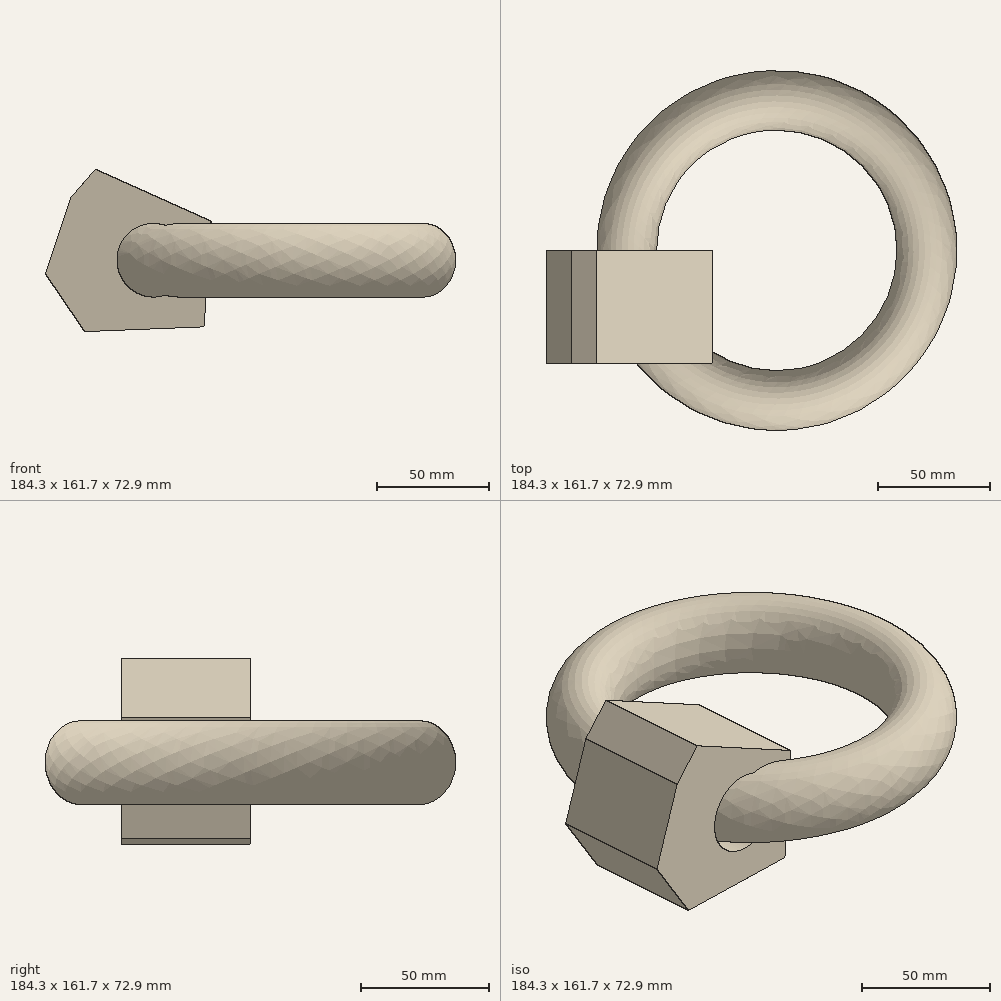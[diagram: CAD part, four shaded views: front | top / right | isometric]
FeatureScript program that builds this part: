
annotation { "Feature Type Name" : "Feature", "Feature Type Description" : "" }
export const myFeature = defineFeature(function(context is Context, id is Id, definition is map)
    precondition{}
    {
        {
            var Q0;
            Q0=qCreatedBy(makeId("Front.planeOp"),FACE);
            var sketch = newSketch(context, id + "F0", { "sketchPlane" : qUnion([Q0])});
            skLineSegment(sketch, "E0", {"start": v(-26.06, 40.83) * mm, "end": v(25.73, 17.6) * mm});
            skLineSegment(sketch, "E1", {"start": v(25.73, 17.6) * mm, "end": v(22.58, -29.88) * mm});
            skLineSegment(sketch, "E2", {"start": v(22.58, -29.88) * mm, "end": v(-31.04, -32.04) * mm});
            skLineSegment(sketch, "E3", {"start": v(-31.04, -32.04) * mm, "end": v(-48.64, -6.14) * mm});
            skLineSegment(sketch, "E4", {"start": v(-48.64, -6.14) * mm, "end": v(-37.35, 27.89) * mm});
            skLineSegment(sketch, "E5", {"start": v(-37.35, 27.89) * mm, "end": v(-26.06, 40.83) * mm});
            skLineSegment(sketch, "E6", {"start": v(54.78, 32.87) * mm, "end": v(54.78, -30.38) * mm});
            skSolve(sketch);
        }
        {
            var Q0;
            Q0=makeQuery(id+"F0.imprint","IMPRINT",FACE,{"disambiguationData":[TD([[makeQuery(id+"F0.imprint","IMPRINT",EDGE,{"derivedFrom":sQuery(id+"F0.wireOp",EDGE,"E0")}),-1.0]])]});
            extrude(context, id + "F1", {"entities" : qUnion([Q0]), "depth" : 50.8 * mm});
        }
        {
            var Q0;
            Q0=makeQuery(id+"F1.opExtrude","CAP_FACE",FACE,{"disambiguationData":[OSD([sQuery(id+"F0.wireOp",EDGE,"E0"),sQuery(id+"F0.wireOp",EDGE,"E1"),sQuery(id+"F0.wireOp",EDGE,"E2"),sQuery(id+"F0.wireOp",EDGE,"E3"),sQuery(id+"F0.wireOp",EDGE,"E4"),sQuery(id+"F0.wireOp",EDGE,"E5")])],"isStart":false});
            var sketch = newSketch(context, id + "F2", { "sketchPlane" : qUnion([Q0])});
            skCircle(sketch, "E7", {"center": v(0, 0) * mm, "radius": 16.54 * mm});
            skSolve(sketch);
        }
        {
            var Q0;
            Q0=makeQuery(id+"F2.imprint","IMPRINT",FACE,{"disambiguationData":[TD([[makeQuery(id+"F2.imprint","IMPRINT",EDGE,{"derivedFrom":sQuery(id+"F2.wireOp",EDGE,"E7")}),1.0]])]});
            extrude(context, id + "F3", {"entities" : qUnion([Q0]), "operationType" : NewBodyOperationType.REMOVE, "oppositeDirection" : true, "depth" : 12.7 * mm});
        }
        {
            var Q0;
            Q0=makeQuery(id+"F3.boolean.opBoolean","COPY",FACE,{"derivedFrom":makeQuery(id+"F3.opExtrude","CAP_FACE",FACE,{"disambiguationData":[OSD([sQuery(id+"F2.wireOp",EDGE,"E7")])],"isStart":false})});
            var Q1;
            Q1=sQuery(id+"F0.wireOp",EDGE,"E6");
            revolve(context, id + "F4", {"entities" : qUnion([Q0]), "axis" : qUnion([Q1]), "revolveType" : RevolveType.FULL});
        }
    });
